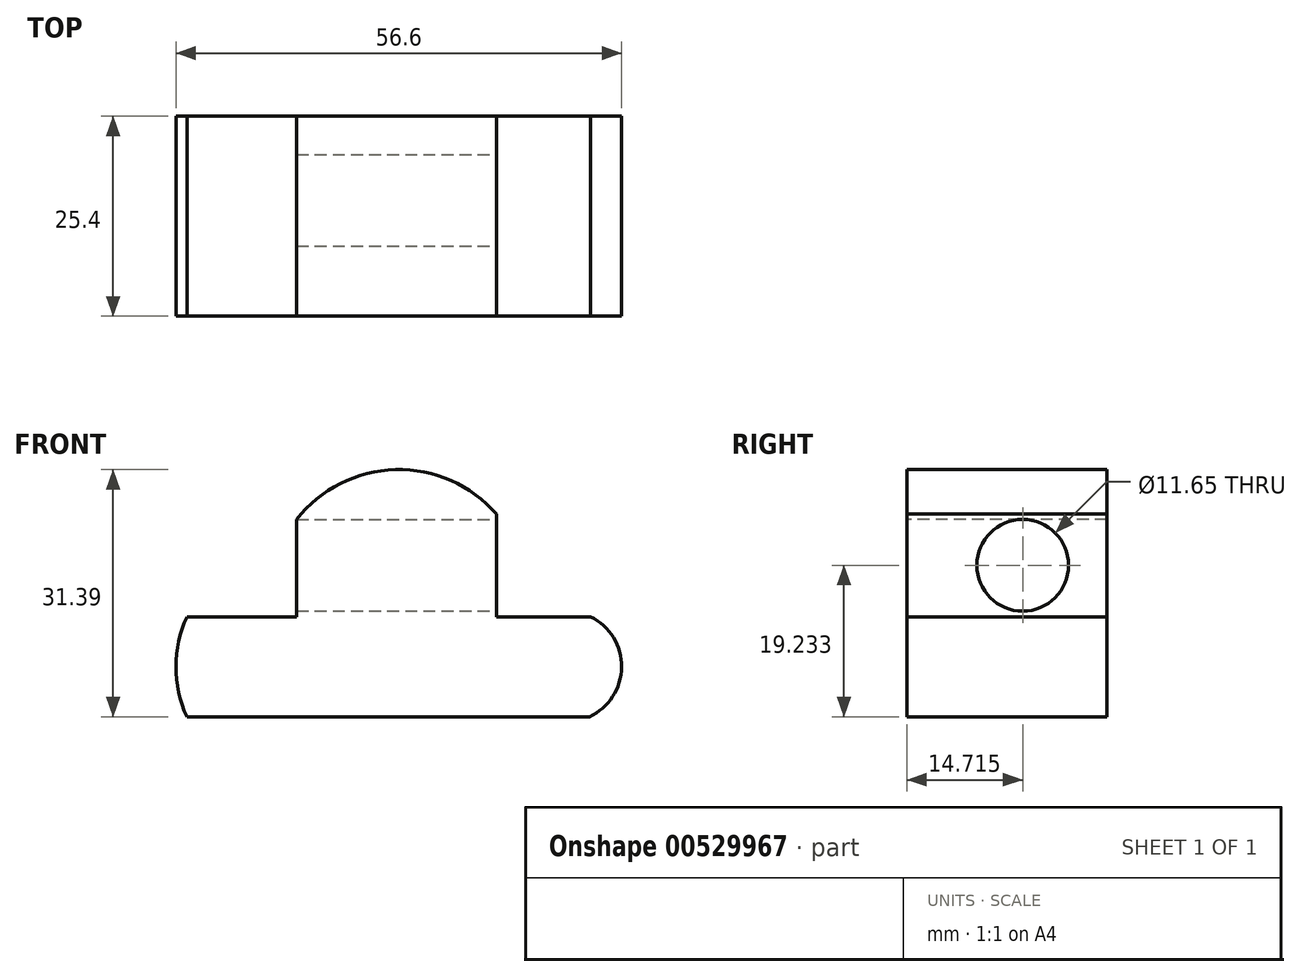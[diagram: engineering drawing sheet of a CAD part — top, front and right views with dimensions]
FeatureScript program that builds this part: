
annotation { "Feature Type Name" : "Feature", "Feature Type Description" : "" }
export const myFeature = defineFeature(function(context is Context, id is Id, definition is map)
    precondition{}
    {
        {
            var Q0;
            Q0=qCreatedBy(makeId("Front.planeOp"),FACE);
            var sketch = newSketch(context, id + "F0", { "sketchPlane" : qUnion([Q0])});
            skLineSegment(sketch, "E0", {"start": v(-29.68, 0) * mm, "end": v(33.82, 0) * mm});
            skLineSegment(sketch, "E1", {"start": v(33.82, 0) * mm, "end": v(33.82, 12.7) * mm});
            skLineSegment(sketch, "E2", {"start": v(33.82, 12.7) * mm, "end": v(17.9, 12.7) * mm});
            skLineSegment(sketch, "E3", {"start": v(17.9, 12.7) * mm, "end": v(17.9, 31.75) * mm});
            skLineSegment(sketch, "E4", {"start": v(17.9, 31.75) * mm, "end": v(-7.5, 31.75) * mm});
            skLineSegment(sketch, "E5", {"start": v(-7.5, 31.75) * mm, "end": v(-7.5, 12.7) * mm});
            skLineSegment(sketch, "E6", {"start": v(-7.5, 12.7) * mm, "end": v(-28.42, 12.7) * mm});
            skLineSegment(sketch, "E7", {"start": v(-28.42, 12.7) * mm, "end": v(-29.68, 0) * mm});
            skSolve(sketch);
        }
        {
            var Q0;
            Q0 = qSketchRegion(id + "F0", true);
            var Q1;
            Q1=makeQuery(id+"F0.imprint","IMPRINT",FACE,{"disambiguationData":[TD([[makeQuery(id+"F0.imprint","IMPRINT",EDGE,{"derivedFrom":sQuery(id+"F0.wireOp",EDGE,"E0")}),1.0]])]});
            extrude(context, id + "F1", {"entities" : qUnion([Q0, Q1]), "depth" : 25.4 * mm, "offsetDistance" : 25.4 * mm});
        }
        {
            var Q0;
            Q0=makeQuery(id+"F1.opExtrude","CAP_FACE",FACE,{"disambiguationData":[OSD([sQuery(id+"F0.wireOp",EDGE,"E0"),sQuery(id+"F0.wireOp",EDGE,"E1"),sQuery(id+"F0.wireOp",EDGE,"E2"),sQuery(id+"F0.wireOp",EDGE,"E3"),sQuery(id+"F0.wireOp",EDGE,"E4"),sQuery(id+"F0.wireOp",EDGE,"E5"),sQuery(id+"F0.wireOp",EDGE,"E6"),sQuery(id+"F0.wireOp",EDGE,"E7")])],"isStart":false});
            var sketch = newSketch(context, id + "F2", { "sketchPlane" : qUnion([Q0])});
            skLineSegment(sketch, "E8", {"start": v(-28.42, 12.7) * mm, "end": v(-28.42, 0) * mm});
            skSolve(sketch);
        }
        {
            var Q0;
            Q0 = qSketchRegion(id + "F2", true);
            var Q1;
            {var subQ0=sQuery(id+"F2.wireOp",EDGE,"E8");Q1=makeQuery(id+"F2.imprint","IMPRINT",FACE,{"disambiguationData":[TD([[makeQuery(id+"F2.imprint","IMPRINT",EDGE,{"derivedFrom":subQ0}),-1.0]])]});}
            extrude(context, id + "F3", {"entities" : qUnion([Q0, Q1]), "operationType" : NewBodyOperationType.REMOVE, "oppositeDirection" : true, "depth" : 25.4 * mm, "offsetDistance" : 25.4 * mm});
        }
        {
            var Q0;
            Q0=makeQuery(id+"F1.opExtrude","CAP_FACE",FACE,{"disambiguationData":[OSD([sQuery(id+"F0.wireOp",EDGE,"E0"),sQuery(id+"F0.wireOp",EDGE,"E1"),sQuery(id+"F0.wireOp",EDGE,"E2"),sQuery(id+"F0.wireOp",EDGE,"E3"),sQuery(id+"F0.wireOp",EDGE,"E4"),sQuery(id+"F0.wireOp",EDGE,"E5"),sQuery(id+"F0.wireOp",EDGE,"E6"),sQuery(id+"F0.wireOp",EDGE,"E7")])],"isStart":false});
            var sketch = newSketch(context, id + "F4", { "sketchPlane" : qUnion([Q0])});
            skLineSegment(sketch, "E9", {"start": v(-24.36, 12.7) * mm, "end": v(-24.36, 0) * mm});
            skSolve(sketch);
        }
        {
            var Q0;
            Q0 = qSketchRegion(id + "F4", true);
            var Q1;
            {var subQ0=sQuery(id+"F4.wireOp",EDGE,"E9");Q1=makeQuery(id+"F4.imprint","IMPRINT",FACE,{"disambiguationData":[TD([[makeQuery(id+"F4.imprint","IMPRINT",EDGE,{"derivedFrom":subQ0}),-1.0]])]});}
            extrude(context, id + "F5", {"entities" : qUnion([Q0, Q1]), "operationType" : NewBodyOperationType.REMOVE, "oppositeDirection" : true, "depth" : 25.4 * mm, "offsetDistance" : 25.4 * mm});
        }
        {
            var Q0;
            Q0=makeQuery(id+"F1.opExtrude","CAP_FACE",FACE,{"disambiguationData":[OSD([sQuery(id+"F0.wireOp",EDGE,"E0"),sQuery(id+"F0.wireOp",EDGE,"E1"),sQuery(id+"F0.wireOp",EDGE,"E2"),sQuery(id+"F0.wireOp",EDGE,"E3"),sQuery(id+"F0.wireOp",EDGE,"E4"),sQuery(id+"F0.wireOp",EDGE,"E5"),sQuery(id+"F0.wireOp",EDGE,"E6"),sQuery(id+"F0.wireOp",EDGE,"E7")])],"isStart":false});
            var sketch = newSketch(context, id + "F6", { "sketchPlane" : qUnion([Q0])});
            skArc(sketch, "E10", {"start": v(17.9, 25.73) * mm, "mid": v(5.03, 31.38) * mm, "end": v(-7.5, 25.05) * mm});
            skSolve(sketch);
        }
        {
            var Q0;
            Q0 = qSketchRegion(id + "F6", true);
            var Q1;
            {var subQ0=sQuery(id+"F6.wireOp",EDGE,"E10");Q1=makeQuery(id+"F6.imprint","IMPRINT",FACE,{"disambiguationData":[TD([[makeQuery(id+"F6.imprint","IMPRINT",EDGE,{"derivedFrom":subQ0}),-1.0]])]});}
            extrude(context, id + "F7", {"entities" : qUnion([Q0, Q1]), "operationType" : NewBodyOperationType.REMOVE, "oppositeDirection" : true, "depth" : 25.4 * mm, "offsetDistance" : 25.4 * mm});
        }
        {
            var Q0;
            Q0=makeQuery(id+"F1.opExtrude","CAP_FACE",FACE,{"disambiguationData":[OSD([sQuery(id+"F0.wireOp",EDGE,"E0"),sQuery(id+"F0.wireOp",EDGE,"E1"),sQuery(id+"F0.wireOp",EDGE,"E2"),sQuery(id+"F0.wireOp",EDGE,"E3"),sQuery(id+"F0.wireOp",EDGE,"E4"),sQuery(id+"F0.wireOp",EDGE,"E5"),sQuery(id+"F0.wireOp",EDGE,"E6"),sQuery(id+"F0.wireOp",EDGE,"E7")])],"isStart":false});
            var sketch = newSketch(context, id + "F8", { "sketchPlane" : qUnion([Q0])});
            skArc(sketch, "E11", {"start": v(-20.6, 12.7) * mm, "mid": v(-24.55, 6.59) * mm, "end": v(-21.46, 0) * mm});
            skSolve(sketch);
        }
        {
            var Q0;
            Q0 = qSketchRegion(id + "F8", true);
            var Q1;
            {var subQ0=sQuery(id+"F8.wireOp",EDGE,"E11");var subQ1=makeQuery(id+"F1.opExtrude","CAP_EDGE",EDGE,{"disambiguationData":[OSD([sQuery(id+"F0.wireOp",EDGE,"E0")])],"isStart":false});var subQ2=makeQuery(id+"F8.imprint","INTERSECT",VERTEX,{"derivedFrom":[subQ1,subQ0]});Q1=makeQuery(id+"F8.imprint","IMPRINT",FACE,{"disambiguationData":[TD([[makeQuery(id+"F8.imprint","IMPRINT",EDGE,{"disambiguationData":[TD([[subQ2,1.0]])],"derivedFrom":subQ0}),-1.0]])]});}
            extrude(context, id + "F9", {"entities" : qUnion([Q0, Q1]), "operationType" : NewBodyOperationType.REMOVE, "oppositeDirection" : true, "depth" : 25.4 * mm, "offsetDistance" : 25.4 * mm});
        }
        {
            var Q0;
            Q0=makeQuery(id+"F1.opExtrude","CAP_FACE",FACE,{"disambiguationData":[OSD([sQuery(id+"F0.wireOp",EDGE,"E0"),sQuery(id+"F0.wireOp",EDGE,"E1"),sQuery(id+"F0.wireOp",EDGE,"E2"),sQuery(id+"F0.wireOp",EDGE,"E3"),sQuery(id+"F0.wireOp",EDGE,"E4"),sQuery(id+"F0.wireOp",EDGE,"E5"),sQuery(id+"F0.wireOp",EDGE,"E6"),sQuery(id+"F0.wireOp",EDGE,"E7")])],"isStart":false});
            var sketch = newSketch(context, id + "F10", { "sketchPlane" : qUnion([Q0])});
            skArc(sketch, "E12", {"start": v(-21.46, 12.7) * mm, "mid": v(-22.84, 6.35) * mm, "end": v(-21.46, 0) * mm});
            skSolve(sketch);
        }
        {
            var Q0;
            Q0 = qSketchRegion(id + "F10", true);
            var Q1;
            {var subQ0=sQuery(id+"F10.wireOp",EDGE,"E12");Q1=makeQuery(id+"F10.imprint","IMPRINT",FACE,{"disambiguationData":[TD([[makeQuery(id+"F10.imprint","IMPRINT",EDGE,{"derivedFrom":subQ0}),-1.0]])]});}
            extrude(context, id + "F11", {"entities" : qUnion([Q0, Q1]), "operationType" : NewBodyOperationType.REMOVE, "oppositeDirection" : true, "depth" : 25.4 * mm, "offsetDistance" : 25.4 * mm});
        }
        {
            var Q0;
            Q0=makeQuery(id+"F1.opExtrude","CAP_FACE",FACE,{"disambiguationData":[OSD([sQuery(id+"F0.wireOp",EDGE,"E0"),sQuery(id+"F0.wireOp",EDGE,"E1"),sQuery(id+"F0.wireOp",EDGE,"E2"),sQuery(id+"F0.wireOp",EDGE,"E3"),sQuery(id+"F0.wireOp",EDGE,"E4"),sQuery(id+"F0.wireOp",EDGE,"E5"),sQuery(id+"F0.wireOp",EDGE,"E6"),sQuery(id+"F0.wireOp",EDGE,"E7")])],"isStart":false});
            var sketch = newSketch(context, id + "F12", { "sketchPlane" : qUnion([Q0])});
            skArc(sketch, "E13", {"start": v(29.66, 0) * mm, "mid": v(33.76, 6.3) * mm, "end": v(29.83, 12.7) * mm});
            skSolve(sketch);
        }
        {
            var Q0;
            Q0 = qSketchRegion(id + "F12", true);
            var Q1;
            {var subQ0=sQuery(id+"F12.wireOp",EDGE,"E13");Q1=makeQuery(id+"F12.imprint","IMPRINT",FACE,{"disambiguationData":[TD([[makeQuery(id+"F12.imprint","IMPRINT",EDGE,{"derivedFrom":subQ0}),-1.0]])]});}
            extrude(context, id + "F13", {"entities" : qUnion([Q0, Q1]), "operationType" : NewBodyOperationType.REMOVE, "oppositeDirection" : true, "depth" : 25.4 * mm, "offsetDistance" : 25.4 * mm});
        }
        {
            var Q0;
            Q0=makeQuery(id+"F1.opExtrude","SWEPT_FACE",FACE,{"disambiguationData":[OSD([sQuery(id+"F0.wireOp",EDGE,"E3")])]});
            var sketch = newSketch(context, id + "F14", { "sketchPlane" : qUnion([Q0])});
            skCircle(sketch, "E14", {"center": v(-10.69, 19.23) * mm, "radius": 5.82 * mm});
            skSolve(sketch);
        }
        {
            var Q0;
            Q0=makeQuery(id+"F14.imprint","IMPRINT",FACE,{"disambiguationData":[TD([[makeQuery(id+"F14.imprint","IMPRINT",EDGE,{"derivedFrom":sQuery(id+"F14.wireOp",EDGE,"E14")}),1.0]])]});
            extrude(context, id + "F15", {"entities" : qUnion([Q0]), "operationType" : NewBodyOperationType.REMOVE, "oppositeDirection" : true, "depth" : 25.4 * mm, "offsetDistance" : 25.4 * mm});
        }
    });
